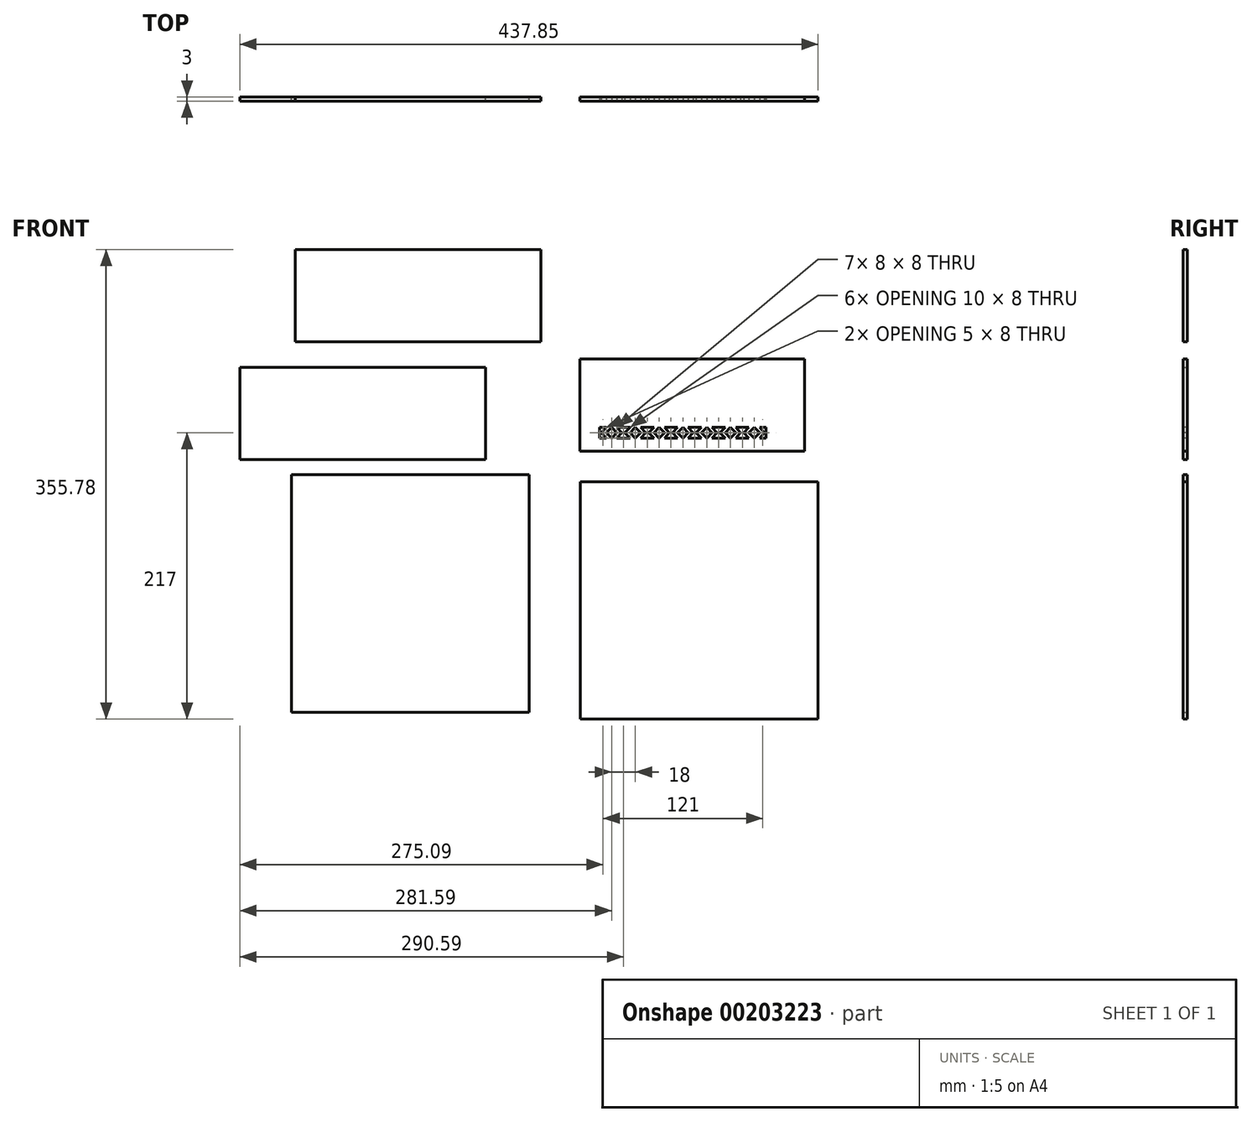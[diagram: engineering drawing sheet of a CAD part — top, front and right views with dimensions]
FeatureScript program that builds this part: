
annotation { "Feature Type Name" : "Feature", "Feature Type Description" : "" }
export const myFeature = defineFeature(function(context is Context, id is Id, definition is map)
    precondition{}
    {
        {
            var Q0;
            Q0=qCreatedBy(makeId("Front.planeOp"),FACE);
            var sketch = newSketch(context, id + "F0", { "sketchPlane" : qUnion([Q0])});
            skLineSegment(sketch, "E0.bottom", {"start": v(-57.26, 85.33) * mm, "end": v(112.74, 85.33) * mm});
            skLineSegment(sketch, "E0.top", {"start": v(-57.26, 15.33) * mm, "end": v(112.74, 15.33) * mm});
            skLineSegment(sketch, "E0.left", {"start": v(-57.26, 85.33) * mm, "end": v(-57.26, 15.33) * mm});
            skLineSegment(sketch, "E0.right", {"start": v(112.74, 85.33) * mm, "end": v(112.74, 15.33) * mm});
            skSolve(sketch);
        }
        {
            var Q0;
            Q0=makeQuery(id+"F0.imprint","IMPRINT",FACE,{"disambiguationData":[TD([[makeQuery(id+"F0.imprint","IMPRINT",EDGE,{"derivedFrom":sQuery(id+"F0.wireOp",EDGE,"E0.bottom")}),-1.0]])]});
            extrude(context, id + "F1", {"entities" : qUnion([Q0]), "depth" : 3 * mm});
        }
        {
            var Q0;
            Q0=makeQuery(id+"F1.opExtrude","CAP_FACE",FACE,{"disambiguationData":[OSD([sQuery(id+"F0.wireOp",EDGE,"E0.bottom"),sQuery(id+"F0.wireOp",EDGE,"E0.top"),sQuery(id+"F0.wireOp",EDGE,"E0.left"),sQuery(id+"F0.wireOp",EDGE,"E0.right")])],"isStart":false});
            var sketch = newSketch(context, id + "F2", { "sketchPlane" : qUnion([Q0])});
            skLineSegment(sketch, "E1", {"start": v(-57.26, 25.36) * mm, "end": v(-42.26, 25.36) * mm, "construction": true});
            skLineSegment(sketch, "E2", {"start": v(-42.26, 25.36) * mm, "end": v(-42.26, 33.36) * mm});
            skLineSegment(sketch, "E3", {"start": v(-42.26, 25.36) * mm, "end": v(-37.26, 25.36) * mm});
            skLineSegment(sketch, "E4", {"start": v(-37.26, 25.36) * mm, "end": v(-41.26, 29.36) * mm});
            skLineSegment(sketch, "E5", {"start": v(-41.26, 29.36) * mm, "end": v(-37.26, 33.36) * mm});
            skLineSegment(sketch, "E6", {"start": v(-37.26, 33.36) * mm, "end": v(-42.26, 33.36) * mm});
            skLineSegment(sketch, "E7", {"start": v(-42.26, 29.36) * mm, "end": v(-41.26, 29.36) * mm, "construction": true});
            skLineSegment(sketch, "E8", {"start": v(-37.26, 25.36) * mm, "end": v(-33.26, 25.36) * mm, "construction": true});
            skLineSegment(sketch, "E9", {"start": v(-33.26, 25.36) * mm, "end": v(-37.26, 29.37) * mm});
            skLineSegment(sketch, "E10", {"start": v(-37.26, 29.37) * mm, "end": v(-33.26, 33.36) * mm});
            skLineSegment(sketch, "E11", {"start": v(-33.26, 33.36) * mm, "end": v(-29.26, 29.37) * mm});
            skLineSegment(sketch, "E12", {"start": v(-29.26, 29.37) * mm, "end": v(-33.26, 25.36) * mm});
            skLineSegment(sketch, "E13", {"start": v(-37.26, 29.37) * mm, "end": v(-29.26, 29.37) * mm, "construction": true});
            skLineSegment(sketch, "E14", {"start": v(-33.26, 25.36) * mm, "end": v(-29.26, 25.36) * mm, "construction": true});
            skLineSegment(sketch, "E15", {"start": v(-29.26, 25.36) * mm, "end": v(-25.57, 29.36) * mm});
            skLineSegment(sketch, "E16", {"start": v(-25.57, 29.36) * mm, "end": v(-29.26, 33.36) * mm});
            skLineSegment(sketch, "E17", {"start": v(-29.26, 33.36) * mm, "end": v(-24.26, 33.36) * mm});
            skLineSegment(sketch, "E18", {"start": v(-24.26, 33.36) * mm, "end": v(-24.26, 25.36) * mm});
            skLineSegment(sketch, "E19", {"start": v(-24.26, 25.36) * mm, "end": v(-29.26, 25.36) * mm});
            skLineSegment(sketch, "E20", {"start": v(-25.57, 29.36) * mm, "end": v(-24.26, 29.36) * mm, "construction": true});
            skLineSegment(sketch, "E21.1.0.0", {"start": v(-19.26, 33.36) * mm, "end": v(-24.26, 33.36) * mm});
            skLineSegment(sketch, "E21.1.0.1", {"start": v(-24.26, 25.36) * mm, "end": v(-24.26, 33.36) * mm});
            skLineSegment(sketch, "E21.1.0.2", {"start": v(-15.26, 33.36) * mm, "end": v(-11.26, 29.37) * mm});
            skLineSegment(sketch, "E21.1.0.3", {"start": v(-23.26, 29.36) * mm, "end": v(-19.26, 33.36) * mm});
            skLineSegment(sketch, "E21.1.0.4", {"start": v(-11.26, 25.36) * mm, "end": v(-7.57, 29.36) * mm});
            skLineSegment(sketch, "E21.1.0.5", {"start": v(-7.57, 29.36) * mm, "end": v(-11.26, 33.36) * mm});
            skLineSegment(sketch, "E21.1.0.6", {"start": v(-24.26, 25.36) * mm, "end": v(-19.26, 25.36) * mm});
            skLineSegment(sketch, "E21.1.0.7", {"start": v(-15.26, 25.36) * mm, "end": v(-11.26, 25.36) * mm, "construction": true});
            skLineSegment(sketch, "E21.1.0.8", {"start": v(-19.26, 29.37) * mm, "end": v(-15.26, 33.36) * mm});
            skLineSegment(sketch, "E21.1.0.9", {"start": v(-19.26, 25.36) * mm, "end": v(-23.26, 29.36) * mm});
            skLineSegment(sketch, "E21.1.0.10", {"start": v(-19.26, 29.37) * mm, "end": v(-11.26, 29.37) * mm, "construction": true});
            skLineSegment(sketch, "E21.1.0.11", {"start": v(-15.26, 25.36) * mm, "end": v(-19.26, 29.37) * mm});
            skLineSegment(sketch, "E21.1.0.12", {"start": v(-11.26, 29.37) * mm, "end": v(-15.26, 25.36) * mm});
            skLineSegment(sketch, "E21.1.0.13", {"start": v(-19.26, 25.36) * mm, "end": v(-15.26, 25.36) * mm, "construction": true});
            skLineSegment(sketch, "E21.1.0.14", {"start": v(-6.26, 33.36) * mm, "end": v(-6.26, 25.36) * mm});
            skLineSegment(sketch, "E21.1.0.15", {"start": v(-6.26, 25.36) * mm, "end": v(-11.26, 25.36) * mm});
            skLineSegment(sketch, "E21.1.0.16", {"start": v(-11.26, 33.36) * mm, "end": v(-6.26, 33.36) * mm});
            skLineSegment(sketch, "E21.1.0.17", {"start": v(-7.57, 29.36) * mm, "end": v(-6.26, 29.36) * mm, "construction": true});
            skLineSegment(sketch, "E21.1.0.18", {"start": v(-24.26, 29.36) * mm, "end": v(-23.26, 29.36) * mm, "construction": true});
            skLineSegment(sketch, "E21.2.0.0", {"start": v(-1.26, 33.36) * mm, "end": v(-6.26, 33.36) * mm});
            skLineSegment(sketch, "E21.2.0.1", {"start": v(-6.26, 25.36) * mm, "end": v(-6.26, 33.36) * mm});
            skLineSegment(sketch, "E21.2.0.2", {"start": v(2.74, 33.36) * mm, "end": v(6.74, 29.37) * mm});
            skLineSegment(sketch, "E21.2.0.3", {"start": v(-5.26, 29.36) * mm, "end": v(-1.26, 33.36) * mm});
            skLineSegment(sketch, "E21.2.0.4", {"start": v(6.74, 25.36) * mm, "end": v(10.43, 29.36) * mm});
            skLineSegment(sketch, "E21.2.0.5", {"start": v(10.43, 29.36) * mm, "end": v(6.74, 33.36) * mm});
            skLineSegment(sketch, "E21.2.0.6", {"start": v(-6.26, 25.36) * mm, "end": v(-1.26, 25.36) * mm});
            skLineSegment(sketch, "E21.2.0.7", {"start": v(2.74, 25.36) * mm, "end": v(6.74, 25.36) * mm, "construction": true});
            skLineSegment(sketch, "E21.2.0.8", {"start": v(-1.26, 29.37) * mm, "end": v(2.74, 33.36) * mm});
            skLineSegment(sketch, "E21.2.0.9", {"start": v(-1.26, 25.36) * mm, "end": v(-5.26, 29.36) * mm});
            skLineSegment(sketch, "E21.2.0.10", {"start": v(-1.26, 29.37) * mm, "end": v(6.74, 29.37) * mm, "construction": true});
            skLineSegment(sketch, "E21.2.0.11", {"start": v(2.74, 25.36) * mm, "end": v(-1.26, 29.37) * mm});
            skLineSegment(sketch, "E21.2.0.12", {"start": v(6.74, 29.37) * mm, "end": v(2.74, 25.36) * mm});
            skLineSegment(sketch, "E21.2.0.13", {"start": v(-1.26, 25.36) * mm, "end": v(2.74, 25.36) * mm, "construction": true});
            skLineSegment(sketch, "E21.2.0.14", {"start": v(11.74, 33.36) * mm, "end": v(11.74, 25.36) * mm});
            skLineSegment(sketch, "E21.2.0.15", {"start": v(11.74, 25.36) * mm, "end": v(6.74, 25.36) * mm});
            skLineSegment(sketch, "E21.2.0.16", {"start": v(6.74, 33.36) * mm, "end": v(11.74, 33.36) * mm});
            skLineSegment(sketch, "E21.2.0.17", {"start": v(10.43, 29.36) * mm, "end": v(11.74, 29.36) * mm, "construction": true});
            skLineSegment(sketch, "E21.2.0.18", {"start": v(-6.26, 29.36) * mm, "end": v(-5.26, 29.36) * mm, "construction": true});
            skLineSegment(sketch, "E21.3.0.0", {"start": v(16.74, 33.36) * mm, "end": v(11.74, 33.36) * mm});
            skLineSegment(sketch, "E21.3.0.1", {"start": v(11.74, 25.36) * mm, "end": v(11.74, 33.36) * mm});
            skLineSegment(sketch, "E21.3.0.2", {"start": v(20.74, 33.36) * mm, "end": v(24.74, 29.37) * mm});
            skLineSegment(sketch, "E21.3.0.3", {"start": v(12.74, 29.36) * mm, "end": v(16.74, 33.36) * mm});
            skLineSegment(sketch, "E21.3.0.4", {"start": v(24.74, 25.36) * mm, "end": v(28.43, 29.36) * mm});
            skLineSegment(sketch, "E21.3.0.5", {"start": v(28.43, 29.36) * mm, "end": v(24.74, 33.36) * mm});
            skLineSegment(sketch, "E21.3.0.6", {"start": v(11.74, 25.36) * mm, "end": v(16.74, 25.36) * mm});
            skLineSegment(sketch, "E21.3.0.7", {"start": v(20.74, 25.36) * mm, "end": v(24.74, 25.36) * mm, "construction": true});
            skLineSegment(sketch, "E21.3.0.8", {"start": v(16.74, 29.37) * mm, "end": v(20.74, 33.36) * mm});
            skLineSegment(sketch, "E21.3.0.9", {"start": v(16.74, 25.36) * mm, "end": v(12.74, 29.36) * mm});
            skLineSegment(sketch, "E21.3.0.10", {"start": v(16.74, 29.37) * mm, "end": v(24.74, 29.37) * mm, "construction": true});
            skLineSegment(sketch, "E21.3.0.11", {"start": v(20.74, 25.36) * mm, "end": v(16.74, 29.37) * mm});
            skLineSegment(sketch, "E21.3.0.12", {"start": v(24.74, 29.37) * mm, "end": v(20.74, 25.36) * mm});
            skLineSegment(sketch, "E21.3.0.13", {"start": v(16.74, 25.36) * mm, "end": v(20.74, 25.36) * mm, "construction": true});
            skLineSegment(sketch, "E21.3.0.14", {"start": v(29.74, 33.36) * mm, "end": v(29.74, 25.36) * mm});
            skLineSegment(sketch, "E21.3.0.15", {"start": v(29.74, 25.36) * mm, "end": v(24.74, 25.36) * mm});
            skLineSegment(sketch, "E21.3.0.16", {"start": v(24.74, 33.36) * mm, "end": v(29.74, 33.36) * mm});
            skLineSegment(sketch, "E21.3.0.17", {"start": v(28.43, 29.36) * mm, "end": v(29.74, 29.36) * mm, "construction": true});
            skLineSegment(sketch, "E21.3.0.18", {"start": v(11.74, 29.36) * mm, "end": v(12.74, 29.36) * mm, "construction": true});
            skLineSegment(sketch, "E21.4.0.0", {"start": v(34.74, 33.36) * mm, "end": v(29.74, 33.36) * mm});
            skLineSegment(sketch, "E21.4.0.1", {"start": v(29.74, 25.36) * mm, "end": v(29.74, 33.36) * mm});
            skLineSegment(sketch, "E21.4.0.2", {"start": v(38.74, 33.36) * mm, "end": v(42.74, 29.37) * mm});
            skLineSegment(sketch, "E21.4.0.3", {"start": v(30.74, 29.36) * mm, "end": v(34.74, 33.36) * mm});
            skLineSegment(sketch, "E21.4.0.4", {"start": v(42.74, 25.36) * mm, "end": v(46.43, 29.36) * mm});
            skLineSegment(sketch, "E21.4.0.5", {"start": v(46.43, 29.36) * mm, "end": v(42.74, 33.36) * mm});
            skLineSegment(sketch, "E21.4.0.6", {"start": v(29.74, 25.36) * mm, "end": v(34.74, 25.36) * mm});
            skLineSegment(sketch, "E21.4.0.7", {"start": v(38.74, 25.36) * mm, "end": v(42.74, 25.36) * mm, "construction": true});
            skLineSegment(sketch, "E21.4.0.8", {"start": v(34.74, 29.37) * mm, "end": v(38.74, 33.36) * mm});
            skLineSegment(sketch, "E21.4.0.9", {"start": v(34.74, 25.36) * mm, "end": v(30.74, 29.36) * mm});
            skLineSegment(sketch, "E21.4.0.10", {"start": v(34.74, 29.37) * mm, "end": v(42.74, 29.37) * mm, "construction": true});
            skLineSegment(sketch, "E21.4.0.11", {"start": v(38.74, 25.36) * mm, "end": v(34.74, 29.37) * mm});
            skLineSegment(sketch, "E21.4.0.12", {"start": v(42.74, 29.37) * mm, "end": v(38.74, 25.36) * mm});
            skLineSegment(sketch, "E21.4.0.13", {"start": v(34.74, 25.36) * mm, "end": v(38.74, 25.36) * mm, "construction": true});
            skLineSegment(sketch, "E21.4.0.14", {"start": v(47.74, 33.36) * mm, "end": v(47.74, 25.36) * mm});
            skLineSegment(sketch, "E21.4.0.15", {"start": v(47.74, 25.36) * mm, "end": v(42.74, 25.36) * mm});
            skLineSegment(sketch, "E21.4.0.16", {"start": v(42.74, 33.36) * mm, "end": v(47.74, 33.36) * mm});
            skLineSegment(sketch, "E21.4.0.17", {"start": v(46.43, 29.36) * mm, "end": v(47.74, 29.36) * mm, "construction": true});
            skLineSegment(sketch, "E21.4.0.18", {"start": v(29.74, 29.36) * mm, "end": v(30.74, 29.36) * mm, "construction": true});
            skLineSegment(sketch, "E21.5.0.0", {"start": v(52.74, 33.36) * mm, "end": v(47.74, 33.36) * mm});
            skLineSegment(sketch, "E21.5.0.1", {"start": v(47.74, 25.36) * mm, "end": v(47.74, 33.36) * mm});
            skLineSegment(sketch, "E21.5.0.2", {"start": v(56.74, 33.36) * mm, "end": v(60.74, 29.37) * mm});
            skLineSegment(sketch, "E21.5.0.3", {"start": v(48.74, 29.36) * mm, "end": v(52.74, 33.36) * mm});
            skLineSegment(sketch, "E21.5.0.4", {"start": v(60.74, 25.36) * mm, "end": v(64.43, 29.36) * mm});
            skLineSegment(sketch, "E21.5.0.5", {"start": v(64.43, 29.36) * mm, "end": v(60.74, 33.36) * mm});
            skLineSegment(sketch, "E21.5.0.6", {"start": v(47.74, 25.36) * mm, "end": v(52.74, 25.36) * mm});
            skLineSegment(sketch, "E21.5.0.7", {"start": v(56.74, 25.36) * mm, "end": v(60.74, 25.36) * mm, "construction": true});
            skLineSegment(sketch, "E21.5.0.8", {"start": v(52.74, 29.37) * mm, "end": v(56.74, 33.36) * mm});
            skLineSegment(sketch, "E21.5.0.9", {"start": v(52.74, 25.36) * mm, "end": v(48.74, 29.36) * mm});
            skLineSegment(sketch, "E21.5.0.10", {"start": v(52.74, 29.37) * mm, "end": v(60.74, 29.37) * mm, "construction": true});
            skLineSegment(sketch, "E21.5.0.11", {"start": v(56.74, 25.36) * mm, "end": v(52.74, 29.37) * mm});
            skLineSegment(sketch, "E21.5.0.12", {"start": v(60.74, 29.37) * mm, "end": v(56.74, 25.36) * mm});
            skLineSegment(sketch, "E21.5.0.13", {"start": v(52.74, 25.36) * mm, "end": v(56.74, 25.36) * mm, "construction": true});
            skLineSegment(sketch, "E21.5.0.14", {"start": v(65.74, 33.36) * mm, "end": v(65.74, 25.36) * mm});
            skLineSegment(sketch, "E21.5.0.15", {"start": v(65.74, 25.36) * mm, "end": v(60.74, 25.36) * mm});
            skLineSegment(sketch, "E21.5.0.16", {"start": v(60.74, 33.36) * mm, "end": v(65.74, 33.36) * mm});
            skLineSegment(sketch, "E21.5.0.17", {"start": v(64.43, 29.36) * mm, "end": v(65.74, 29.36) * mm, "construction": true});
            skLineSegment(sketch, "E21.5.0.18", {"start": v(47.74, 29.36) * mm, "end": v(48.74, 29.36) * mm, "construction": true});
            skLineSegment(sketch, "E21.6.0.0", {"start": v(70.74, 33.36) * mm, "end": v(65.74, 33.36) * mm});
            skLineSegment(sketch, "E21.6.0.1", {"start": v(65.74, 25.36) * mm, "end": v(65.74, 33.36) * mm});
            skLineSegment(sketch, "E21.6.0.2", {"start": v(74.74, 33.36) * mm, "end": v(78.74, 29.37) * mm});
            skLineSegment(sketch, "E21.6.0.3", {"start": v(66.74, 29.36) * mm, "end": v(70.74, 33.36) * mm});
            skLineSegment(sketch, "E21.6.0.4", {"start": v(78.74, 25.36) * mm, "end": v(82.43, 29.36) * mm});
            skLineSegment(sketch, "E21.6.0.5", {"start": v(82.43, 29.36) * mm, "end": v(78.74, 33.36) * mm});
            skLineSegment(sketch, "E21.6.0.6", {"start": v(65.74, 25.36) * mm, "end": v(70.74, 25.36) * mm});
            skLineSegment(sketch, "E21.6.0.7", {"start": v(74.74, 25.36) * mm, "end": v(78.74, 25.36) * mm, "construction": true});
            skLineSegment(sketch, "E21.6.0.8", {"start": v(70.74, 29.37) * mm, "end": v(74.74, 33.36) * mm});
            skLineSegment(sketch, "E21.6.0.9", {"start": v(70.74, 25.36) * mm, "end": v(66.74, 29.36) * mm});
            skLineSegment(sketch, "E21.6.0.10", {"start": v(70.74, 29.37) * mm, "end": v(78.74, 29.37) * mm, "construction": true});
            skLineSegment(sketch, "E21.6.0.11", {"start": v(74.74, 25.36) * mm, "end": v(70.74, 29.37) * mm});
            skLineSegment(sketch, "E21.6.0.12", {"start": v(78.74, 29.37) * mm, "end": v(74.74, 25.36) * mm});
            skLineSegment(sketch, "E21.6.0.13", {"start": v(70.74, 25.36) * mm, "end": v(74.74, 25.36) * mm, "construction": true});
            skLineSegment(sketch, "E21.6.0.14", {"start": v(83.74, 33.36) * mm, "end": v(83.74, 25.36) * mm});
            skLineSegment(sketch, "E21.6.0.15", {"start": v(83.74, 25.36) * mm, "end": v(78.74, 25.36) * mm});
            skLineSegment(sketch, "E21.6.0.16", {"start": v(78.74, 33.36) * mm, "end": v(83.74, 33.36) * mm});
            skLineSegment(sketch, "E21.6.0.17", {"start": v(82.43, 29.36) * mm, "end": v(83.74, 29.36) * mm, "construction": true});
            skLineSegment(sketch, "E21.6.0.18", {"start": v(65.74, 29.36) * mm, "end": v(66.74, 29.36) * mm, "construction": true});
            skLineSegment(sketch, "E21.direction1", {"start": v(-42.26, 25.36) * mm, "end": v(-24.26, 25.36) * mm, "construction": true});
            skSolve(sketch);
        }
        {
            var Q0;
            Q0 = qSketchRegion(id + "F2", true);
            var Q1;
            {var subQ0=sQuery(id+"F2.wireOp",EDGE,"2vZWt5Fo-VWEp-dLN9-v5xc-DNbKKBRj0eA0");Q1=makeQuery(id+"F2.imprint","IMPRINT",FACE,{"disambiguationData":[TD([[makeQuery(id+"F2.imprint","IMPRINT",EDGE,{"derivedFrom":subQ0}),-1.0]])]});}
            extrude(context, id + "F3", {"entities" : qUnion([Q0, Q1]), "operationType" : NewBodyOperationType.REMOVE, "oppositeDirection" : true, "depth" : 25 * mm});
        }
        {
            var Q0;
            Q0=qCreatedBy(makeId("Front.planeOp"),FACE);
            var sketch = newSketch(context, id + "F4", { "sketchPlane" : qUnion([Q0])});
            skLineSegment(sketch, "E22.bottom", {"start": v(-314.85, 79.02) * mm, "end": v(-128.85, 79.02) * mm});
            skLineSegment(sketch, "E22.top", {"start": v(-314.85, 9.02) * mm, "end": v(-128.85, 9.02) * mm});
            skLineSegment(sketch, "E22.left", {"start": v(-314.85, 79.02) * mm, "end": v(-314.85, 9.02) * mm});
            skLineSegment(sketch, "E22.right", {"start": v(-128.85, 79.02) * mm, "end": v(-128.85, 9.02) * mm});
            skSolve(sketch);
        }
        {
            var Q0;
            Q0=makeQuery(id+"F4.imprint","IMPRINT",FACE,{"disambiguationData":[TD([[makeQuery(id+"F4.imprint","IMPRINT",EDGE,{"derivedFrom":sQuery(id+"F4.wireOp",EDGE,"E22.bottom")}),-1.0]])]});
            extrude(context, id + "F5", {"entities" : qUnion([Q0]), "depth" : 3 * mm});
        }
        {
            var Q0;
            Q0=qCreatedBy(makeId("Front.planeOp"),FACE);
            var sketch = newSketch(context, id + "F6", { "sketchPlane" : qUnion([Q0])});
            skLineSegment(sketch, "E23.bottom", {"start": v(-57, -7.64) * mm, "end": v(123, -7.64) * mm});
            skLineSegment(sketch, "E23.top", {"start": v(-57, -187.64) * mm, "end": v(123, -187.64) * mm});
            skLineSegment(sketch, "E23.left", {"start": v(-57, -7.64) * mm, "end": v(-57, -187.64) * mm});
            skLineSegment(sketch, "E23.right", {"start": v(123, -7.64) * mm, "end": v(123, -187.64) * mm});
            skSolve(sketch);
        }
        {
            var Q0;
            Q0 = qSketchRegion(id + "F6", true);
            var Q1;
            Q1 = qConstructionFilter(qBodyType(qCreatedBy(id + "F6" ,EDGE), BodyType.WIRE), ConstructionObject.NO);
            extrude(context, id + "F7", {"entities" : qUnion([Q0]), "surfaceEntities" : qUnion([Q1]), "depth" : 3 * mm});
        }
        {
            var Q0;
            Q0=qCreatedBy(makeId("Front.planeOp"),FACE);
            var sketch = newSketch(context, id + "F8", { "sketchPlane" : qUnion([Q0])});
            skLineSegment(sketch, "E24.bottom", {"start": v(-272.86, 168.14) * mm, "end": v(-86.86, 168.14) * mm});
            skLineSegment(sketch, "E24.top", {"start": v(-272.86, 98.14) * mm, "end": v(-86.86, 98.14) * mm});
            skLineSegment(sketch, "E24.left", {"start": v(-272.86, 168.14) * mm, "end": v(-272.86, 98.14) * mm});
            skLineSegment(sketch, "E24.right", {"start": v(-86.86, 168.14) * mm, "end": v(-86.86, 98.14) * mm});
            skSolve(sketch);
        }
        {
            var Q0;
            Q0=makeQuery(id+"F8.imprint","IMPRINT",FACE,{"disambiguationData":[TD([[makeQuery(id+"F8.imprint","IMPRINT",EDGE,{"derivedFrom":sQuery(id+"F8.wireOp",EDGE,"E24.bottom")}),-1.0]])]});
            extrude(context, id + "F9", {"entities" : qUnion([Q0]), "depth" : 3 * mm});
        }
        {
            var Q0;
            Q0=qCreatedBy(makeId("Front.planeOp"),FACE);
            var sketch = newSketch(context, id + "F10", { "sketchPlane" : qUnion([Q0])});
            skLineSegment(sketch, "E25.bottom", {"start": v(-275.84, -2.33) * mm, "end": v(-95.84, -2.33) * mm});
            skLineSegment(sketch, "E25.top", {"start": v(-275.84, -182.33) * mm, "end": v(-95.84, -182.33) * mm});
            skLineSegment(sketch, "E25.left", {"start": v(-275.84, -2.33) * mm, "end": v(-275.84, -182.33) * mm});
            skLineSegment(sketch, "E25.right", {"start": v(-95.84, -2.33) * mm, "end": v(-95.84, -182.33) * mm});
            skSolve(sketch);
        }
        {
            var Q0;
            Q0=makeQuery(id+"F10.imprint","IMPRINT",FACE,{"disambiguationData":[TD([[makeQuery(id+"F10.imprint","IMPRINT",EDGE,{"derivedFrom":sQuery(id+"F10.wireOp",EDGE,"E25.bottom")}),-1.0]])]});
            extrude(context, id + "F11", {"entities" : qUnion([Q0]), "depth" : 3 * mm});
        }
    });
